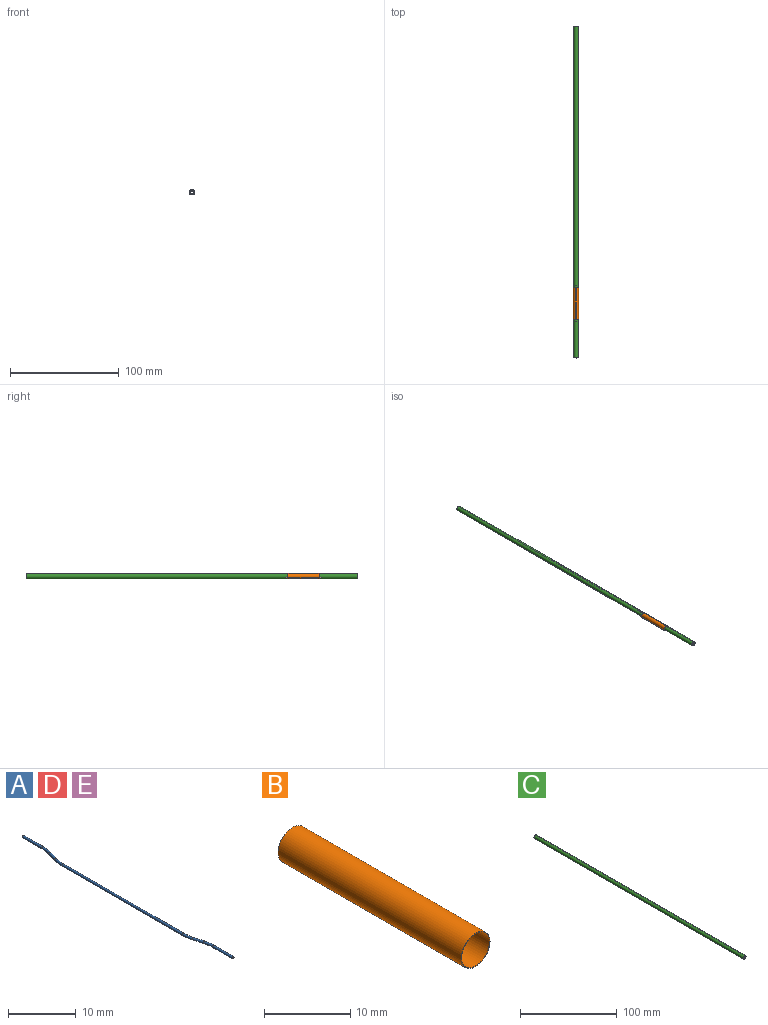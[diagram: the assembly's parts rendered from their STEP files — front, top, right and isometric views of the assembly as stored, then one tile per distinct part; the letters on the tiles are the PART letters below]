
ASSEMBLY  parts=5 mates=4
PART A: 11 faces, bbox 1.5x44x0.4 mm
  f0: plane 0.38x0.38mm, normal (0,-1,0), area 0.1mm2, adj f2
  f1: plane 0.38x0.38mm, normal (0,1,0), area 0.1mm2, adj f10
  f2: cylinder r=0.19mm len=4.11mm, axis (0,1,0), area 4.9mm2, adj f0,f3
  f3: torus R=6.35mm, axis (0,0,1), area 2.1mm2, adj f2,f4
  f4: cylinder r=0.19mm len=1.88mm, axis (-0.28,0.96,0), area 2.2mm2, adj f3,f5
  f5: torus R=6.35mm, axis (0,0,-1), area 2.1mm2, adj f4,f6
  f6: cylinder r=0.19mm len=25.22mm, axis (0,1,0), area 30.2mm2, adj f5,f7
  f7: torus R=6.35mm, axis (0,0,-1), area 2.1mm2, adj f6,f8
  f8: cylinder r=0.19mm len=1.88mm, axis (0.28,0.96,0), area 2.2mm2, adj f7,f9
  f9: torus R=6.35mm, axis (0,0,1), area 2.1mm2, adj f8,f10
  f10: cylinder r=0.19mm len=4.11mm, axis (0,1,0), area 4.9mm2, adj f1,f9
PART B: 4 faces, bbox 4.7x30x4.7 mm
  f0: cylinder r=2.29mm len=30mm, axis (0,1,0), area 430.9mm2, adj f2,f3
  f1: cylinder r=2.36mm len=30mm, axis (0,1,0), area 445.3mm2, adj f2,f3
  f2: plane 4.72x4.72mm, normal (0,-1,0), area 1.1mm2, adj f0,f1
  f3: plane 4.72x4.72mm, normal (0,1,0), area 1.1mm2, adj f0,f1
PART C: 7 faces, bbox 4.3x304.8x4.3 mm
  f0: cylinder r=1.4mm len=304.8mm, axis (0,1,0), area 2675.4mm2, adj f5,f6
  f1: cylinder r=0.19mm len=304.8mm, axis (0,1,0), area 364.8mm2, adj f5,f6
  f2: cylinder r=0.19mm len=304.8mm, axis (0,1,0), area 364.8mm2, adj f5,f6
  f3: cylinder r=0.19mm len=304.8mm, axis (0,1,0), area 364.8mm2, adj f5,f6
  f4: cylinder r=2.16mm len=304.8mm, axis (0,1,0), area 4134.7mm2, adj f5,f6
  f5: plane 4.32x4.32mm, normal (0,-1,0), area 8.2mm2, adj f0,f1,f2,f3,f4
  f6: plane 4.32x4.32mm, normal (0,1,0), area 8.2mm2, adj f0,f1,f2,f3,f4
PART D: same geometry as A
PART E: same geometry as A
PLACE A rot(axis=(0,-1,0),150deg) t=(-49.42,-92.11,19.48)mm
PLACE B t=(-50.96,-55.11,20.36)mm
PLACE C t=(-50.96,184.69,20.36)mm
PLACE D rot(axis=(0,1,0),90deg) t=(-50.96,-92.11,22.14)mm
PLACE E rot(axis=(0,-1,0),30deg) t=(-52.5,-92.11,19.48)mm
MATE cylindrical E.f2 <-> C.f3  axis (0,-1,0) through (-52.5,-92.11,19.48)mm
MATE cylindrical D.f2 <-> C.f1  axis (0,-1,0) through (-50.96,-92.11,22.14)mm
MATE cylindrical B.f0 <-> C.f4  axis (0,-1,0) through (-50.96,-85.11,20.36)mm
MATE cylindrical A.f2 <-> C.f2  axis (0,-1,0) through (-49.42,-92.11,19.48)mm
